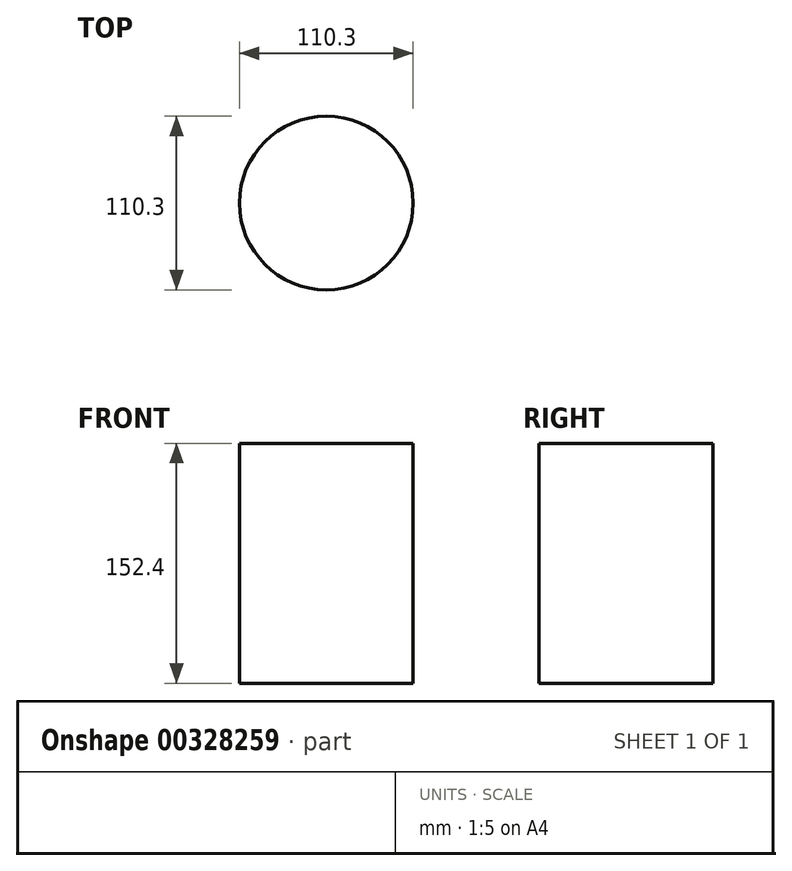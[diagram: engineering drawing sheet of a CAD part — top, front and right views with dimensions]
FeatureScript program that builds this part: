
annotation { "Feature Type Name" : "Feature", "Feature Type Description" : "" }
export const myFeature = defineFeature(function(context is Context, id is Id, definition is map)
    precondition{}
    {
        {
            var Q0;
            Q0=qCreatedBy(makeId("Top.planeOp"),FACE);
            var sketch = newSketch(context, id + "F0", { "sketchPlane" : qUnion([Q0])});
            skCircle(sketch, "E0", {"center": v(0, 0) * mm, "radius": 55.15 * mm});
            skSolve(sketch);
        }
        {
            var Q0;
            Q0=makeQuery(id+"F0.imprint","IMPRINT",FACE,{"disambiguationData":[TD([[makeQuery(id+"F0.imprint","IMPRINT",EDGE,{"derivedFrom":sQuery(id+"F0.wireOp",EDGE,"E0")}),1.0]])]});
            extrude(context, id + "F1", {"entities" : qUnion([Q0]), "depth" : 152.4 * mm});
        }
    });
